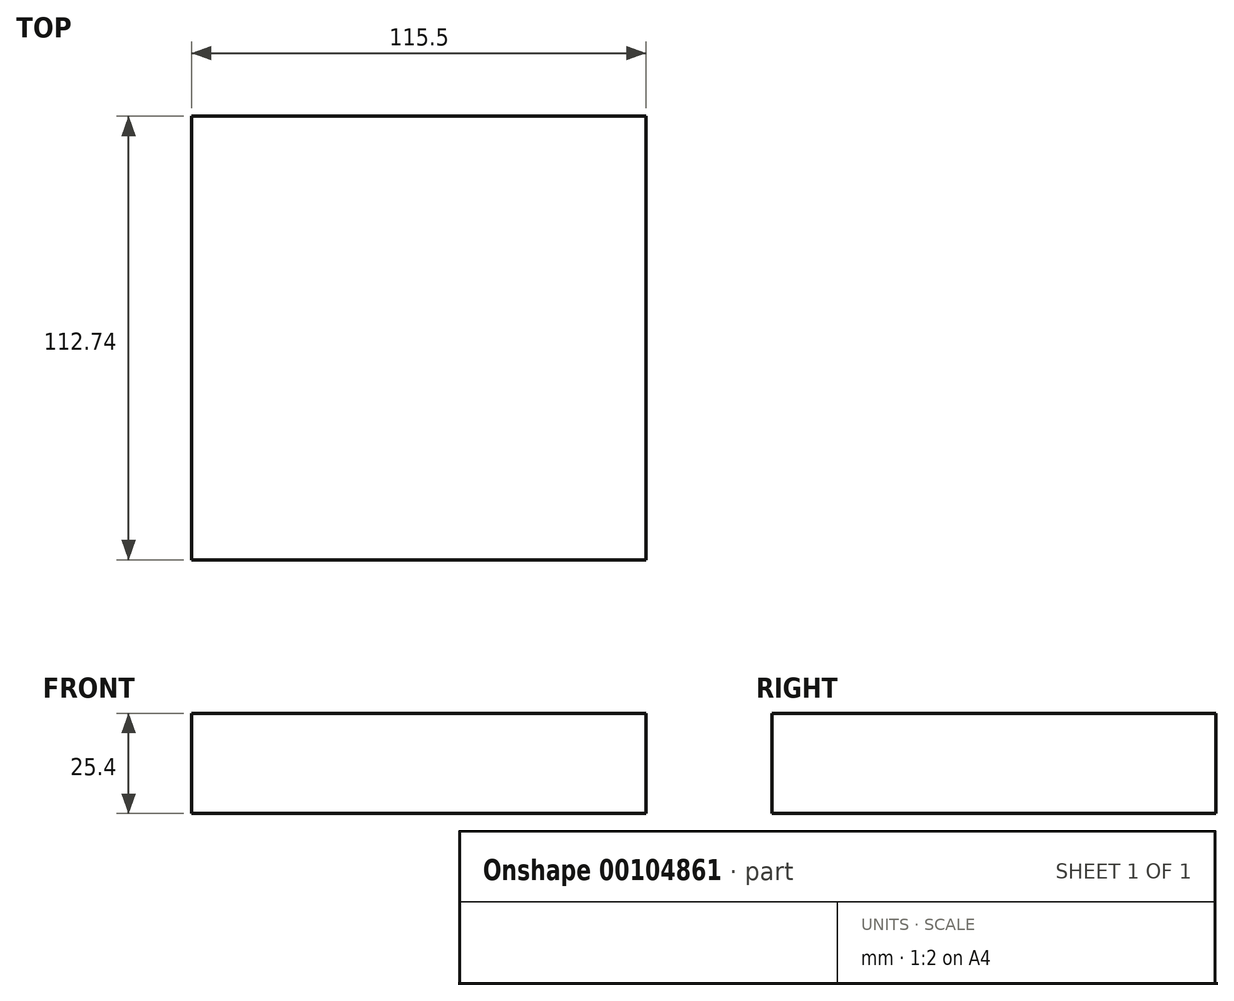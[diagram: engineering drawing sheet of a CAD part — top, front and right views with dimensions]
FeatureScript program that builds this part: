
annotation { "Feature Type Name" : "Feature", "Feature Type Description" : "" }
export const myFeature = defineFeature(function(context is Context, id is Id, definition is map)
    precondition{}
    {
        {
            var Q0;
            Q0=qCreatedBy(makeId("Top.planeOp"),FACE);
            var sketch = newSketch(context, id + "F0", { "sketchPlane" : qUnion([Q0])});
            skLineSegment(sketch, "E0.bottom", {"start": v(-56.84, 59.3) * mm, "end": v(58.66, 59.3) * mm});
            skLineSegment(sketch, "E0.top", {"start": v(-56.84, -53.45) * mm, "end": v(58.66, -53.45) * mm});
            skLineSegment(sketch, "E0.left", {"start": v(-56.84, 59.3) * mm, "end": v(-56.84, -53.45) * mm});
            skLineSegment(sketch, "E0.right", {"start": v(58.66, 59.3) * mm, "end": v(58.66, -53.45) * mm});
            skSolve(sketch);
        }
        {
            var Q0;
            Q0 = qSketchRegion(id + "F0", true);
            extrude(context, id + "F1", {"entities" : qUnion([Q0]), "depth" : 25.4 * mm});
        }
    });
